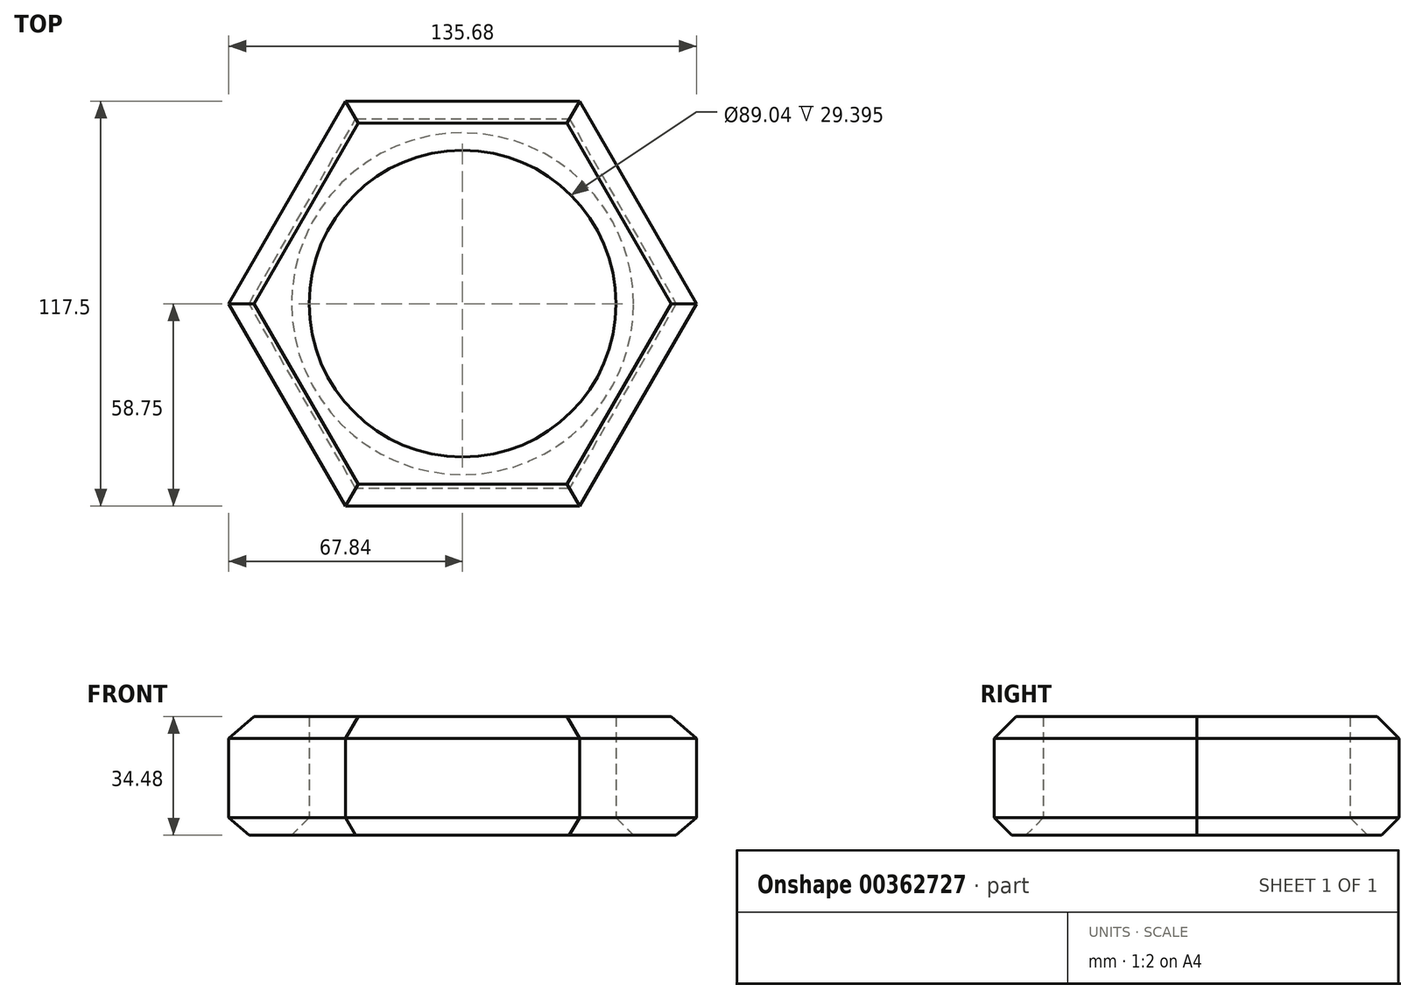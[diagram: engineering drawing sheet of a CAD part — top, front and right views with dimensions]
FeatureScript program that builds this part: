
annotation { "Feature Type Name" : "Feature", "Feature Type Description" : "" }
export const myFeature = defineFeature(function(context is Context, id is Id, definition is map)
    precondition{}
    {
        {
            var Q0;
            Q0=qCreatedBy(makeId("Top.planeOp"),FACE);
            var sketch = newSketch(context, id + "F0", { "sketchPlane" : qUnion([Q0])});
            skCircle(sketch, "E0.cCircle", {"center": v(0, 0) * mm, "radius": 67.84 * mm, "construction": true});
            skLineSegment(sketch, "E0.0", {"start": v(67.84, 0) * mm, "end": v(33.92, -58.75) * mm});
            skLineSegment(sketch, "E0.1", {"start": v(33.92, -58.75) * mm, "end": v(-33.92, -58.75) * mm});
            skLineSegment(sketch, "E0.2", {"start": v(-33.92, -58.75) * mm, "end": v(-67.84, 0) * mm});
            skLineSegment(sketch, "E0.3", {"start": v(-67.84, 0) * mm, "end": v(-33.92, 58.75) * mm});
            skLineSegment(sketch, "E0.4", {"start": v(-33.92, 58.75) * mm, "end": v(33.92, 58.75) * mm});
            skLineSegment(sketch, "E0.5", {"start": v(33.92, 58.75) * mm, "end": v(67.84, 0) * mm});
            skSolve(sketch);
        }
        {
            var Q0;
            Q0=makeQuery(id+"F0.imprint","IMPRINT",FACE,{"disambiguationData":[TD([[makeQuery(id+"F0.imprint","IMPRINT",EDGE,{"derivedFrom":sQuery(id+"F0.wireOp",EDGE,"E0.0")}),-1.0]])]});
            var sketch = newSketch(context, id + "F1", { "sketchPlane" : qUnion([Q0])});
            skCircle(sketch, "E1.0", {"center": v(0, 0) * mm, "radius": 44.52 * mm});
            skSolve(sketch);
        }
        {
            var Q0;
            Q0=makeQuery(id+"F1.imprint","IMPRINT",FACE,{"disambiguationData":[TD([[makeQuery(id+"F1.imprint","IMPRINT",EDGE,{"derivedFrom":sQuery(id+"F1.wireOp",EDGE,"E1.0")}),-1.0]])]});
            extrude(context, id + "F2", {"entities" : qUnion([Q0]), "depth" : 34.48 * mm});
        }
        {
            var Q0;
            Q0=makeQuery(id+"F2.opExtrude","CAP_EDGE",EDGE,{"disambiguationData":[OSD([sQuery(id+"F0.wireOp",EDGE,"E0.4")])],"isStart":false});
            var Q1;
            Q1=makeQuery(id+"F2.opExtrude","CAP_EDGE",EDGE,{"disambiguationData":[OSD([sQuery(id+"F0.wireOp",EDGE,"E0.2")])],"isStart":false});
            var Q2;
            Q2=makeQuery(id+"F2.opExtrude","CAP_EDGE",EDGE,{"disambiguationData":[OSD([sQuery(id+"F0.wireOp",EDGE,"E0.5")])],"isStart":false});
            var Q3;
            Q3=makeQuery(id+"F2.opExtrude","CAP_EDGE",EDGE,{"disambiguationData":[OSD([sQuery(id+"F0.wireOp",EDGE,"E0.1")])],"isStart":false});
            var Q4;
            Q4=makeQuery(id+"F2.opExtrude","CAP_EDGE",EDGE,{"disambiguationData":[OSD([sQuery(id+"F0.wireOp",EDGE,"E0.0")])],"isStart":false});
            var Q5;
            Q5=makeQuery(id+"F2.opExtrude","CAP_EDGE",EDGE,{"disambiguationData":[OSD([sQuery(id+"F0.wireOp",EDGE,"E0.3")])],"isStart":false});
            chamfer(context, id + "F3", {"entities" : qUnion([Q0, Q1, Q2, Q3, Q4, Q5]), "width" : 6.35 * mm, "tangentPropagation" : true});
        }
        {
            var Q0;
            Q0=makeQuery(id+"F2.opExtrude","CAP_EDGE",EDGE,{"disambiguationData":[OSD([sQuery(id+"F0.wireOp",EDGE,"E0.0")])],"isStart":true});
            var Q1;
            Q1=makeQuery(id+"F2.opExtrude","CAP_EDGE",EDGE,{"disambiguationData":[OSD([sQuery(id+"F0.wireOp",EDGE,"E0.5")])],"isStart":true});
            var Q2;
            Q2=makeQuery(id+"F2.opExtrude","CAP_EDGE",EDGE,{"disambiguationData":[OSD([sQuery(id+"F0.wireOp",EDGE,"E0.4")])],"isStart":true});
            var Q3;
            Q3=makeQuery(id+"F2.opExtrude","CAP_EDGE",EDGE,{"disambiguationData":[OSD([sQuery(id+"F0.wireOp",EDGE,"E0.3")])],"isStart":true});
            var Q4;
            Q4=makeQuery(id+"F2.opExtrude","CAP_EDGE",EDGE,{"disambiguationData":[OSD([sQuery(id+"F0.wireOp",EDGE,"E0.2")])],"isStart":true});
            var Q5;
            Q5=makeQuery(id+"F2.opExtrude","CAP_EDGE",EDGE,{"disambiguationData":[OSD([sQuery(id+"F0.wireOp",EDGE,"E0.1")])],"isStart":true});
            var Q6;
            Q6=makeQuery(id+"F2.opExtrude","CAP_EDGE",EDGE,{"disambiguationData":[OSD([sQuery(id+"F1.wireOp",EDGE,"E1.0")])],"isStart":true});
            chamfer(context, id + "F4", {"entities" : qUnion([Q0, Q1, Q2, Q3, Q4, Q5, Q6]), "width" : 5.08 * mm, "tangentPropagation" : true});
        }
    });
